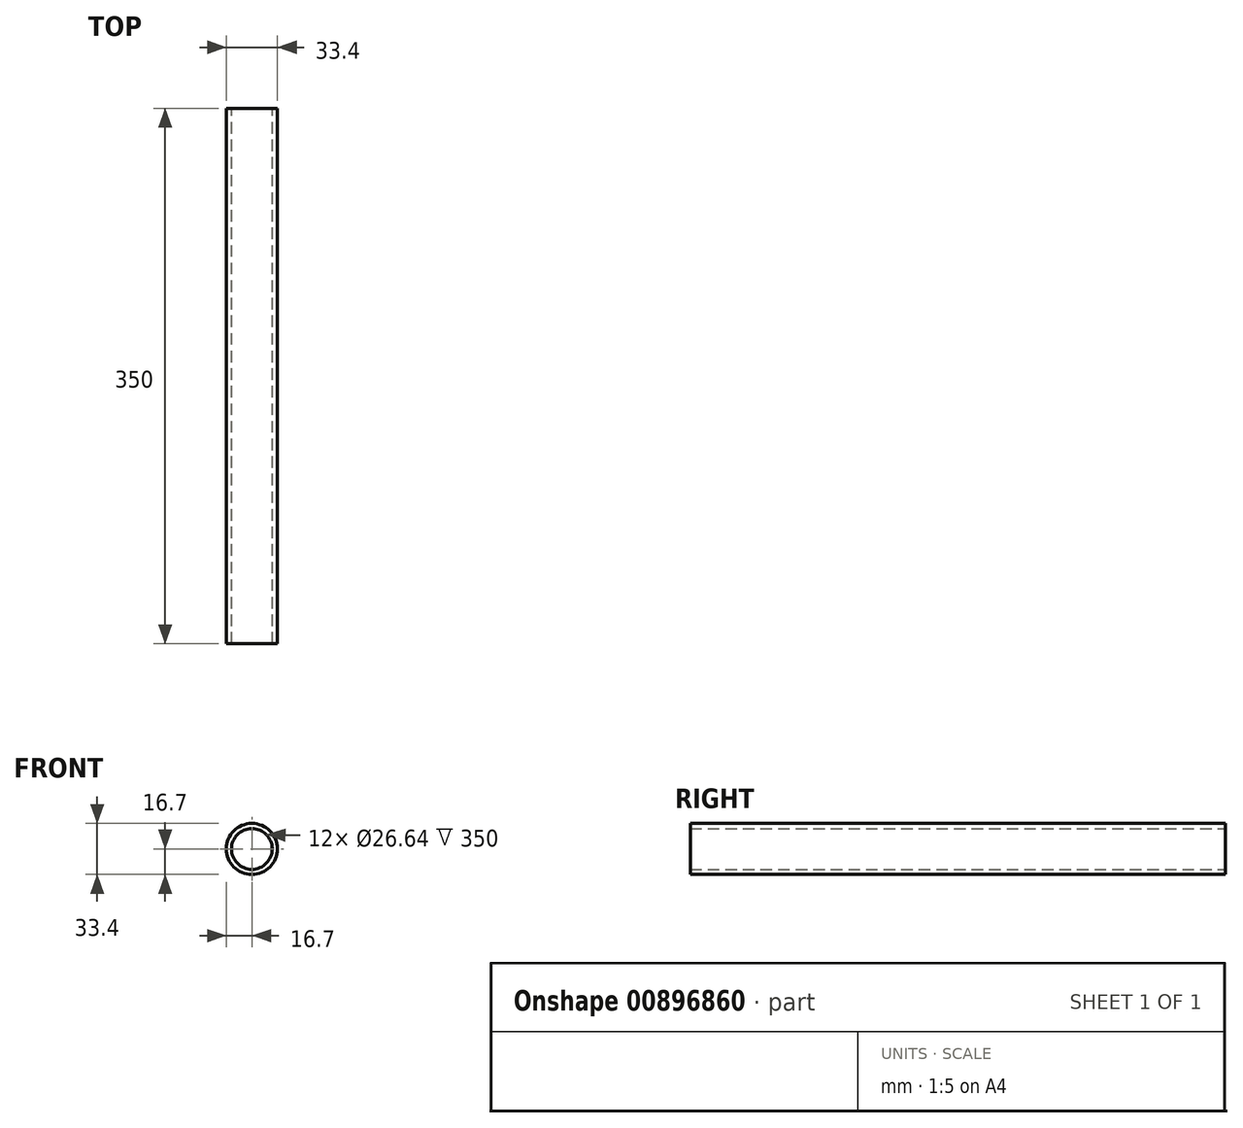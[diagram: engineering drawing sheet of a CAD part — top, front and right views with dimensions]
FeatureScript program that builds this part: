
annotation { "Feature Type Name" : "Feature", "Feature Type Description" : "" }
export const myFeature = defineFeature(function(context is Context, id is Id, definition is map)
    precondition{}
    {
        {
            var Q0;
            Q0=qCreatedBy(makeId("Front.planeOp"),FACE);
            var sketch = newSketch(context, id + "F0", { "sketchPlane" : qUnion([Q0])});
            skCircle(sketch, "E0", {"center": v(0, 0) * mm, "radius": 16.7 * mm});
            skCircle(sketch, "E1", {"center": v(0, 0) * mm, "radius": 13.32 * mm});
            skSolve(sketch);
        }
        {
            var Q0;
            Q0=makeQuery(id+"F0.imprint","IMPRINT",FACE,{"disambiguationData":[TD([[makeQuery(id+"F0.imprint","IMPRINT",EDGE,{"derivedFrom":sQuery(id+"F0.wireOp",EDGE,"E0")}),1.0]])]});
            extrude(context, id + "F1", {"entities" : qUnion([Q0]), "endBound" : BoundingType.SYMMETRIC, "depth" : 350 * mm, "offsetDistance" : 25.4 * mm});
        }
    });
